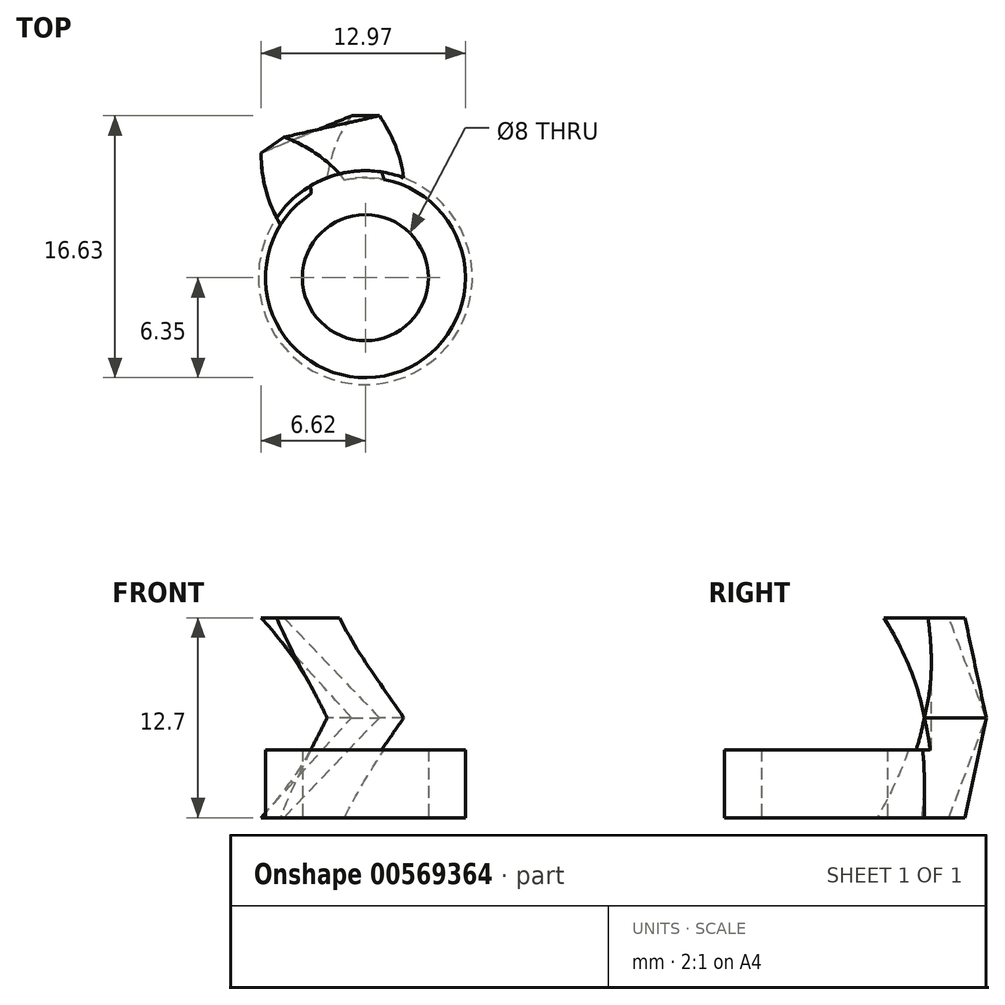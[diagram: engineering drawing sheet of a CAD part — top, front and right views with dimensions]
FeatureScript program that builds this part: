
annotation { "Feature Type Name" : "Feature", "Feature Type Description" : "" }
export const myFeature = defineFeature(function(context is Context, id is Id, definition is map)
    precondition{}
    {
        {
            var Q0;
            Q0=qCreatedBy(makeId("Top.planeOp"),FACE);
            var sketch = newSketch(context, id + "F0", { "sketchPlane" : qUnion([Q0])});
            skCircle(sketch, "E0", {"center": v(0, 0) * mm, "radius": 4 * mm});
            skCircle(sketch, "E1", {"center": v(0, 0) * mm, "radius": 25.4 * mm, "construction": true});
            skLineSegment(sketch, "E2", {"start": v(4.41, 25.01) * mm, "end": v(0, 0) * mm, "construction": true});
            skLineSegment(sketch, "E3", {"start": v(-4.41, 25.01) * mm, "end": v(0, 0) * mm, "construction": true});
            skLineSegment(sketch, "E4", {"start": v(-8.69, 23.87) * mm, "end": v(0, 0) * mm, "construction": true});
            skLineSegment(sketch, "E5", {"start": v(-7.64, 29.81) * mm, "end": v(29.71, 16.22) * mm, "construction": true});
            skLineSegment(sketch, "E6", {"start": v(8.69, 23.87) * mm, "end": v(29.88, 23.87) * mm, "construction": true});
            skLineSegment(sketch, "E7", {"start": v(-8.69, 23.87) * mm, "end": v(-20, 19.75) * mm, "construction": true});
            skLineSegment(sketch, "E8", {"start": v(-4.41, 25.01) * mm, "end": v(-10.92, 23.87) * mm, "construction": true});
            skLineSegment(sketch, "E9", {"start": v(4.41, 25.01) * mm, "end": v(-8.61, 27.31) * mm, "construction": true});
            skArc(sketch, "E10", {"start": v(-8.23, 28.57) * mm, "mid": v(-8.78, 26.25) * mm, "end": v(-8.69, 23.87) * mm});
            skLineSegment(sketch, "E11", {"start": v(0, 0) * mm, "end": v(0, 25.4) * mm, "construction": true});
            skLineSegment(sketch, "E12", {"start": v(0, 25.4) * mm, "end": v(-8.82, 25.4) * mm, "construction": true});
            skLineSegment(sketch, "E13", {"start": v(0, 0) * mm, "end": v(8.69, 23.87) * mm, "construction": true});
            skLineSegment(sketch, "E14", {"start": v(-7.64, 29.81) * mm, "end": v(0, 0) * mm, "construction": true});
            skArc(sketch, "E15.MirrorCS", {"start": v(-6.52, 29) * mm, "mid": v(-4.93, 27.24) * mm, "end": v(-3.86, 25.1) * mm});
            skLineSegment(sketch, "E16", {"start": v(-8.23, 28.57) * mm, "end": v(-6.52, 29) * mm});
            skPoint(sketch, "E17.orphan", {"position": v(-7.64, 29.81) * mm});
            skCircle(sketch, "E18", {"center": v(0, 0) * mm, "radius": 6.35 * mm});
            skArc(sketch, "E19", {"start": v(-6.62, 7.92) * mm, "mid": v(-6.32, 5.55) * mm, "end": v(-5.4, 3.36) * mm});
            skArc(sketch, "E20.MirrorCS", {"start": v(-5.17, 8.93) * mm, "mid": v(-3.06, 7.83) * mm, "end": v(-1.31, 6.21) * mm});
            skLineSegment(sketch, "E21", {"start": v(-6.62, 7.92) * mm, "end": v(-5.17, 8.93) * mm});
            skLineSegment(sketch, "E22", {"start": v(-5.4, 3.36) * mm, "end": v(-5.17, 8.93) * mm, "construction": true});
            skLineSegment(sketch, "E23", {"start": v(-1.31, 6.21) * mm, "end": v(-6.62, 7.92) * mm, "construction": true});
            skLineSegment(sketch, "E24", {"start": v(-5.4, 3.36) * mm, "end": v(-1.31, 6.21) * mm, "construction": true});
            skLineSegment(sketch, "E25", {"start": v(-5.9, 8.42) * mm, "end": v(0, 0) * mm, "construction": true});
            skSolve(sketch);
        }
        {
            var Q0;
            Q0=qCreatedBy(makeId("Top.planeOp"),FACE);
            cPlane(context, id + "F1", {"entities" : qUnion([Q0]), "cplaneType" : CPlaneType.OFFSET, "offset" : 6.35 * mm, "width" : 152.4 * mm, "height" : 152.4 * mm});
        }
        {
            var Q0;
            Q0=makeQuery(id+"F0.imprint","IMPRINT",FACE,{"disambiguationData":[TD([[makeQuery(id+"F0.imprint","IMPRINT",EDGE,{"derivedFrom":sQuery(id+"F0.wireOp",EDGE,"E0")}),-1.0]])]});
            extrude(context, id + "F2", {"entities" : qUnion([Q0]), "depth" : 6.35 * mm, "offsetDistance" : 25.4 * mm});
        }
        {
            var Q0;
            Q0=qCreatedBy(id+"F1.planeOp",FACE);
            var sketch = newSketch(context, id + "F3", { "sketchPlane" : qUnion([Q0])});
            skCircle(sketch, "E26", {"center": v(0, 0) * mm, "radius": 4 * mm});
            skCircle(sketch, "E27", {"center": v(0, 0) * mm, "radius": 25.4 * mm, "construction": true});
            skLineSegment(sketch, "E28", {"start": v(17.96, 17.96) * mm, "end": v(0, 0) * mm, "construction": true});
            skLineSegment(sketch, "E29", {"start": v(10.73, 23.02) * mm, "end": v(0, 0) * mm, "construction": true});
            skLineSegment(sketch, "E30", {"start": v(6.57, 24.53) * mm, "end": v(0, 0) * mm, "construction": true});
            skLineSegment(sketch, "E31", {"start": v(10.84, 28.8) * mm, "end": v(33.64, -3.76) * mm, "construction": true});
            skLineSegment(sketch, "E32", {"start": v(20.8, 14.57) * mm, "end": v(38.16, 2.42) * mm, "construction": true});
            skLineSegment(sketch, "E33", {"start": v(6.57, 24.53) * mm, "end": v(-5.05, 27.65) * mm, "construction": true});
            skLineSegment(sketch, "E34", {"start": v(10.73, 23.02) * mm, "end": v(4.74, 25.81) * mm, "construction": true});
            skLineSegment(sketch, "E35", {"start": v(17.96, 17.96) * mm, "end": v(8.61, 27.31) * mm, "construction": true});
            skArc(sketch, "E36", {"start": v(9.64, 28.12) * mm, "mid": v(7.86, 26.54) * mm, "end": v(6.57, 24.53) * mm});
            skLineSegment(sketch, "E37", {"start": v(0, 0) * mm, "end": v(14.57, 20.8) * mm, "construction": true});
            skLineSegment(sketch, "E38", {"start": v(14.57, 20.8) * mm, "end": v(7.34, 25.87) * mm, "construction": true});
            skLineSegment(sketch, "E39", {"start": v(0, 0) * mm, "end": v(20.8, 14.57) * mm, "construction": true});
            skLineSegment(sketch, "E40", {"start": v(10.84, 28.8) * mm, "end": v(0, 0) * mm, "construction": true});
            skArc(sketch, "E41.MirrorCS", {"start": v(11.3, 27.5) * mm, "mid": v(11.59, 25.14) * mm, "end": v(11.24, 22.78) * mm});
            skLineSegment(sketch, "E42", {"start": v(9.64, 28.12) * mm, "end": v(11.3, 27.5) * mm});
            skPoint(sketch, "E43.orphan", {"position": v(10.84, 28.8) * mm});
            skPoint(sketch, "E44.center", {"position": v(0.53, -18.26) * mm});
            skCircle(sketch, "E45", {"center": v(0, 0) * mm, "radius": 6.35 * mm});
            skArc(sketch, "E46", {"start": v(-0.88, 10.28) * mm, "mid": v(-1.99, 8.17) * mm, "end": v(-2.5, 5.84) * mm});
            skArc(sketch, "E47.MirrorCS", {"start": v(0.88, 10.28) * mm, "mid": v(1.99, 8.17) * mm, "end": v(2.5, 5.84) * mm});
            skLineSegment(sketch, "E48", {"start": v(-0.88, 10.28) * mm, "end": v(0.88, 10.28) * mm});
            skLineSegment(sketch, "E49", {"start": v(-2.5, 5.84) * mm, "end": v(0.88, 10.28) * mm, "construction": true});
            skLineSegment(sketch, "E50", {"start": v(2.5, 5.84) * mm, "end": v(-0.88, 10.28) * mm, "construction": true});
            skLineSegment(sketch, "E51", {"start": v(-2.5, 5.84) * mm, "end": v(2.5, 5.84) * mm, "construction": true});
            skLineSegment(sketch, "E52", {"start": v(0, 10.28) * mm, "end": v(0, 0) * mm, "construction": true});
            skSolve(sketch);
        }
        {
            var Q1;
            {var subQ0=sQuery(id+"F0.wireOp",EDGE,"E19");Q1=makeQuery(id+"F0.imprint","IMPRINT",FACE,{"disambiguationData":[TD([[makeQuery(id+"F0.imprint","IMPRINT",EDGE,{"derivedFrom":subQ0}),1.0]])]});}
            var Q2;
            {var subQ0=sQuery(id+"F3.wireOp",EDGE,"E46");Q2=makeQuery(id+"F3.imprint","IMPRINT",FACE,{"disambiguationData":[TD([[makeQuery(id+"F3.imprint","IMPRINT",EDGE,{"derivedFrom":subQ0}),1.0]])]});}
            loft(context, id + "F4", {"operationType" : NewBodyOperationType.ADD, "sheetProfilesArray" : [{ "sheetProfileEntities" : qUnion([Q1]) }, { "sheetProfileEntities" : qUnion([Q2]) }]});
        }
        {
            var Q0;
            Q0=makeQuery(id+"F2.opExtrude","SWEPT_BODY",BODY,{"disambiguationData":[OSD([sQuery(id+"F0.wireOp",EDGE,"E0"),sQuery(id+"F0.wireOp",EDGE,"E1")])]});
            var Q1;
            {var subQ0=sQuery(id+"FnK1oxyonltIGas_0.wireOp",EDGE,"21216eee-12ac-45d1-9511-a7a3080e9845");Q1=makeQuery(id+"F4.boolean.opBoolean","MERGE",FACE,{"derivedFrom":[makeQuery(id+"F2.opExtrude","CAP_FACE",FACE,{"disambiguationData":[OSD([sQuery(id+"F0.wireOp",EDGE,"E0"),sQuery(id+"F0.wireOp",EDGE,"E1")])],"isStart":false}),makeQuery(id+"F4.opLoft","CAP_FACE",FACE,{"disambiguationData":[OSD([makeQuery(id+"FnK1oxyonltIGas_0.imprint","IMPRINT",FACE,{"disambiguationData":[TD([[makeQuery(id+"FnK1oxyonltIGas_0.imprint","IMPRINT",EDGE,{"derivedFrom":subQ0}),1.0]])]})])],"isStart":true})]});}
            mirror(context, id + "F5", {"operationType" : NewBodyOperationType.ADD, "entities" : qUnion([Q0]), "mirrorPlane" : qUnion([Q1])});
        }
        {
            var Q0;
            {var subQ0=sQuery(id+"F0.wireOp",EDGE,"E19");var subQ1=sQuery(id+"F0.wireOp",EDGE,"E18");var subQ3=makeQuery(id+"F0.imprint","IMPRINT",FACE,{"disambiguationData":[TD([[makeQuery(id+"F0.imprint","IMPRINT",EDGE,{"derivedFrom":subQ0}),1.0]])]});Q0=makeQuery(id+"F5.opPattern","COPY",FACE,{"derivedFrom":makeQuery(id+"FUupeDgjqGhtx0C_1.4.F4.boolean.opBoolean","MERGE",FACE,{"derivedFrom":[makeQuery(id+"FUupeDgjqGhtx0C_1.3.F4.boolean.opBoolean","MERGE",FACE,{"derivedFrom":[makeQuery(id+"FUupeDgjqGhtx0C_1.2.F4.boolean.opBoolean","MERGE",FACE,{"derivedFrom":[makeQuery(id+"FUupeDgjqGhtx0C_1.1.F4.boolean.opBoolean","MERGE",FACE,{"derivedFrom":[makeQuery(id+"F4.boolean.opBoolean","MERGE",FACE,{"derivedFrom":[makeQuery(id+"F2.opExtrude","CAP_FACE",FACE,{"disambiguationData":[OSD([sQuery(id+"F0.wireOp",EDGE,"E0"),subQ1])],"isStart":true}),makeQuery(id+"F4.opLoft","CAP_FACE",FACE,{"disambiguationData":[OSD([subQ3])],"isStart":true})]}),makeQuery(id+"FUupeDgjqGhtx0C_1.1.F4.opLoft","CAP_FACE",FACE,{"disambiguationData":[OSD([subQ3])],"isStart":true})]}),makeQuery(id+"FUupeDgjqGhtx0C_1.2.F4.opLoft","CAP_FACE",FACE,{"disambiguationData":[OSD([subQ3])],"isStart":true})]}),makeQuery(id+"FUupeDgjqGhtx0C_1.3.F4.opLoft","CAP_FACE",FACE,{"disambiguationData":[OSD([subQ3])],"isStart":true})]}),makeQuery(id+"FUupeDgjqGhtx0C_1.4.F4.opLoft","CAP_FACE",FACE,{"disambiguationData":[OSD([subQ3])],"isStart":true})]}),"instanceName":"1"});}
            var sketch = newSketch(context, id + "F6", { "sketchPlane" : qUnion([Q0])});
            skCircle(sketch, "E53", {"center": v(0, 0) * mm, "radius": 6.8 * mm});
            skSolve(sketch);
        }
        {
            var Q0;
            Q0=qSketchRegion(id+"F6",true);
            extrude(context, id + "F7", {"entities" : qUnion([Q0]), "operationType" : NewBodyOperationType.REMOVE, "oppositeDirection" : true, "depth" : 8.38 * mm, "offsetDistance" : 25.4 * mm});
        }
    });
